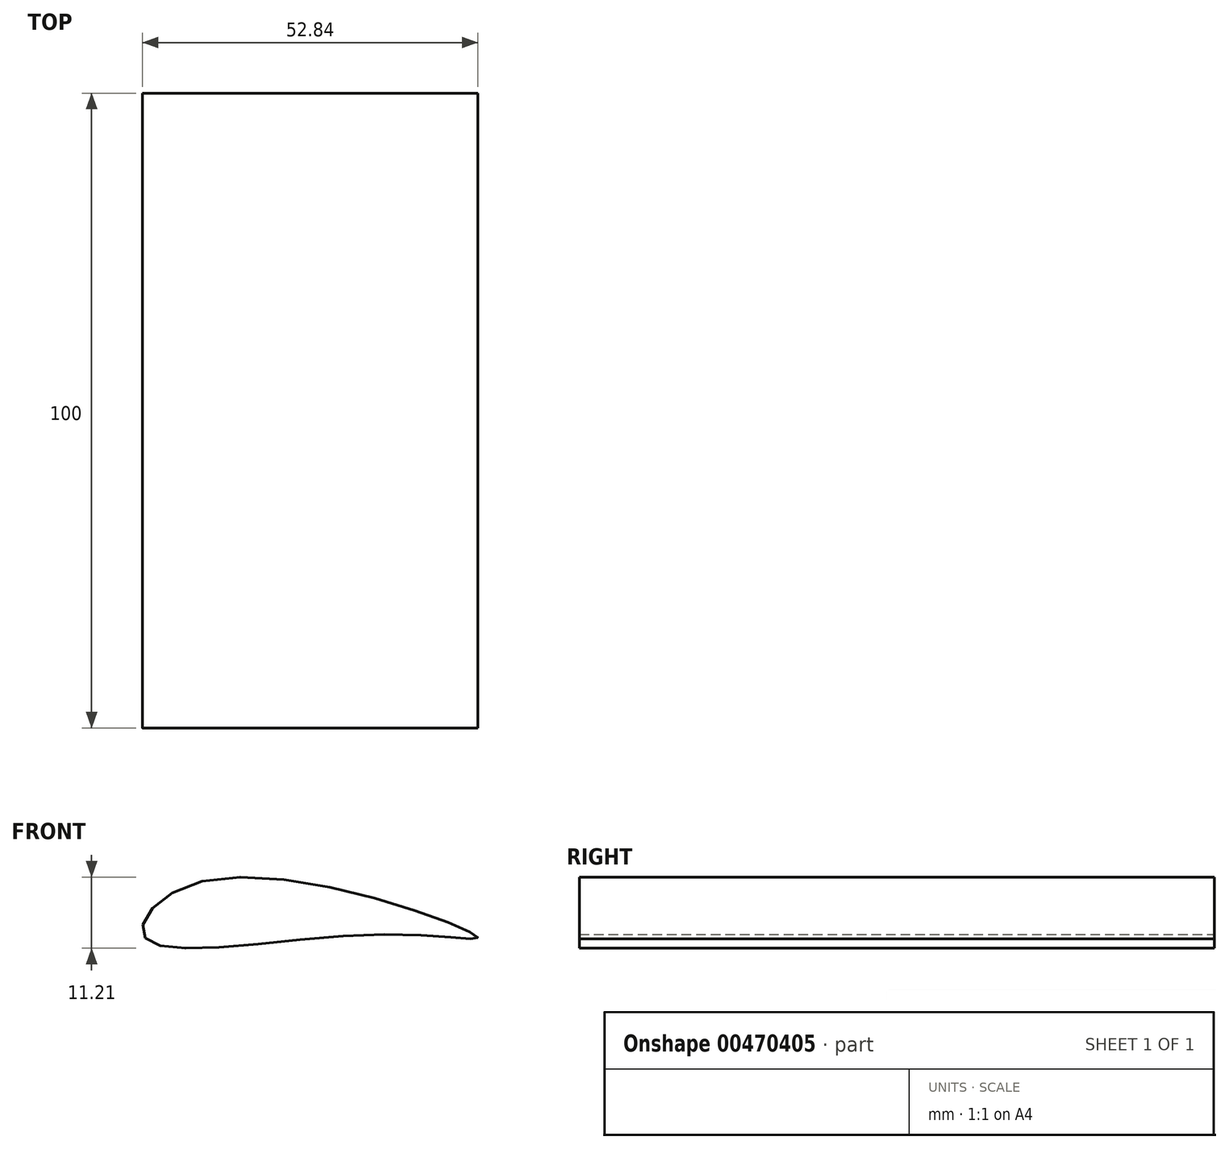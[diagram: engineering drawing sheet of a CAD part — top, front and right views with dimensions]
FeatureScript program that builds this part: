
annotation { "Feature Type Name" : "Feature", "Feature Type Description" : "" }
export const myFeature = defineFeature(function(context is Context, id is Id, definition is map)
    precondition{}
    {
        {
            var Q0;
            Q0=qCreatedBy(makeId("Front.planeOp"),FACE);
            var sketch = newSketch(context, id + "F0", { "sketchPlane" : qUnion([Q0])});
            skFitSpline(sketch, "E0", {"points": [v(-67.42, -6.08) * mm, v(-57.47, 3.04) * mm, v(-15.2, -5.8) * mm, v(-30.12, -5.53) * mm, v(-67.42, -6.08) * mm]});
            skSolve(sketch);
        }
        {
            var Q0;
            Q0 = qSketchRegion(id + "F0", true);
            extrude(context, id + "F1", {"entities" : qUnion([Q0]), "depth" : 100 * mm});
        }
    });
